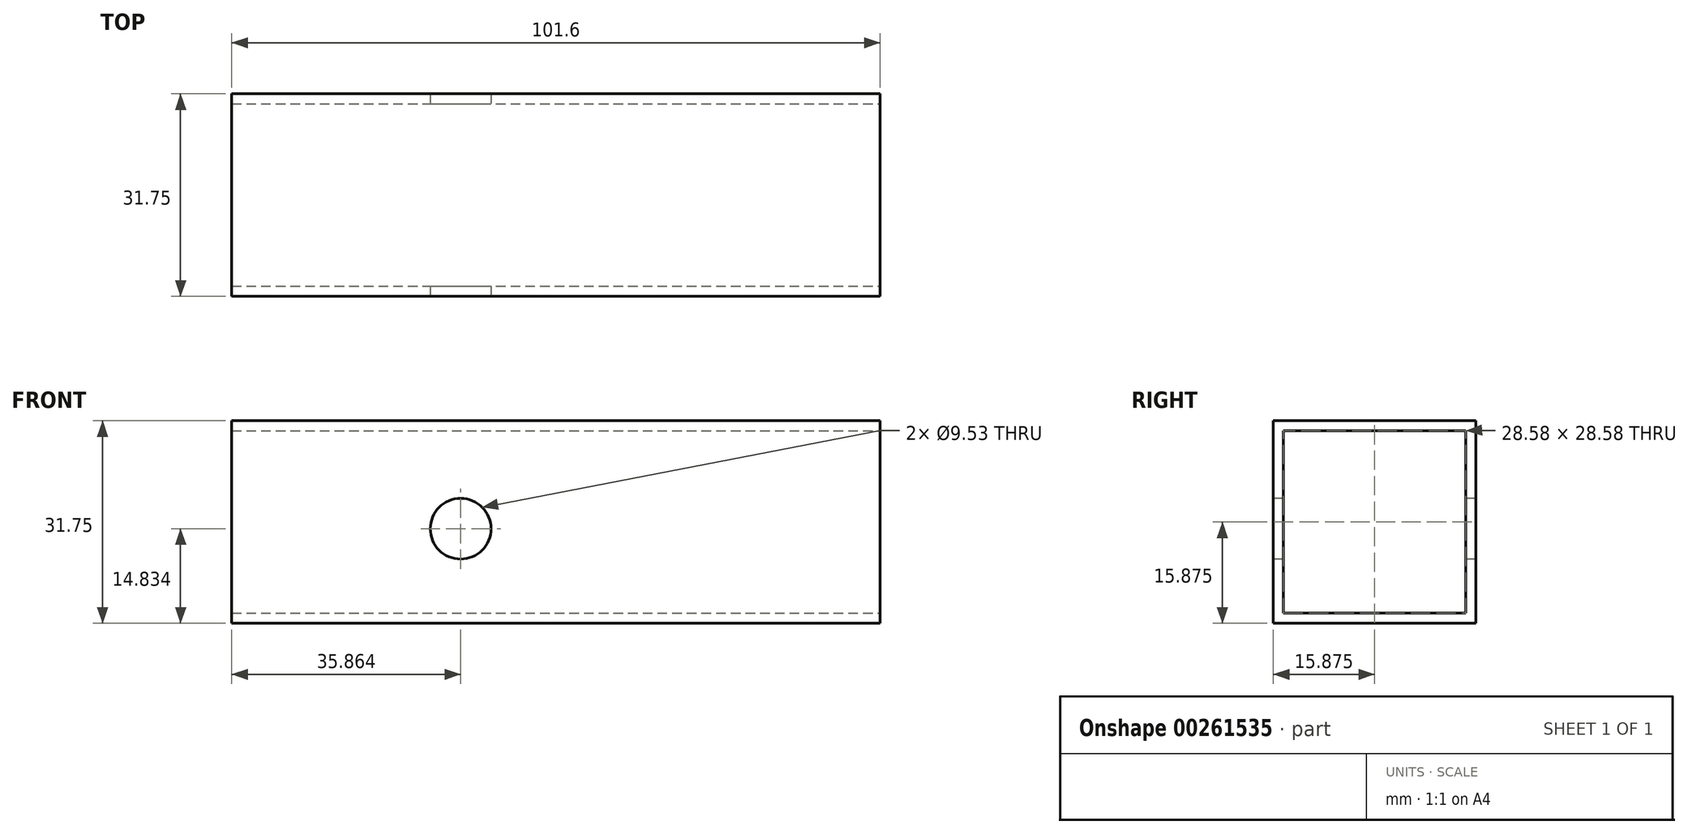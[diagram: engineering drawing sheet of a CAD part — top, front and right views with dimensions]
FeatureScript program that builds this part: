
annotation { "Feature Type Name" : "Feature", "Feature Type Description" : "" }
export const myFeature = defineFeature(function(context is Context, id is Id, definition is map)
    precondition{}
    {
        {
            var Q0;
            Q0=qCreatedBy(makeId("Top.planeOp"),FACE);
            var sketch = newSketch(context, id + "F0", { "sketchPlane" : qUnion([Q0])});
            skLineSegment(sketch, "E0.bottom", {"start": v(0, 0) * mm, "end": v(-101.6, 0) * mm});
            skLineSegment(sketch, "E0.top", {"start": v(0, 31.75) * mm, "end": v(-101.6, 31.75) * mm});
            skLineSegment(sketch, "E0.left", {"start": v(0, 0) * mm, "end": v(0, 31.75) * mm});
            skLineSegment(sketch, "E0.right", {"start": v(-101.6, 0) * mm, "end": v(-101.6, 31.75) * mm});
            skSolve(sketch);
        }
        {
            var Q0;
            Q0=makeQuery(id+"F0.imprint","IMPRINT",FACE,{"disambiguationData":[TD([[makeQuery(id+"F0.imprint","IMPRINT",EDGE,{"derivedFrom":sQuery(id+"F0.wireOp",EDGE,"E0.bottom")}),-1.0]])]});
            extrude(context, id + "F1", {"entities" : qUnion([Q0]), "depth" : 31.75 * mm});
        }
        {
            var Q0;
            Q0=makeQuery(id+"F1.opExtrude","SWEPT_FACE",FACE,{"disambiguationData":[OSD([sQuery(id+"F0.wireOp",EDGE,"E0.right")])]});
            var Q1;
            Q1=makeQuery(id+"F1.opExtrude","SWEPT_FACE",FACE,{"disambiguationData":[OSD([sQuery(id+"F0.wireOp",EDGE,"E0.left")])]});
            shell(context, id + "F2", {"entities" : qUnion([Q0, Q1]), "thickness" : 1.59 * mm});
        }
        {
            var Q0;
            Q0=makeQuery(id+"F1.opExtrude","CAP_FACE",FACE,{"disambiguationData":[OSD([sQuery(id+"F0.wireOp",EDGE,"E0.bottom"),sQuery(id+"F0.wireOp",EDGE,"E0.top"),sQuery(id+"F0.wireOp",EDGE,"E0.left"),sQuery(id+"F0.wireOp",EDGE,"E0.right")])],"isStart":false});
            var sketch = newSketch(context, id + "F3", { "sketchPlane" : qUnion([Q0])});
            skCircle(sketch, "E1", {"center": v(-35.86, 16.92) * mm, "radius": 4.76 * mm});
            skSolve(sketch);
        }
        {
            var Q0;
            Q0=sQuery(id+"F3.wireOp",VERTEX,"E1.center");
            var Q1;
            Q1=makeQuery(id+"F1.opExtrude","SWEPT_BODY",BODY,{"disambiguationData":[OSD([sQuery(id+"F0.wireOp",EDGE,"E0.bottom"),sQuery(id+"F0.wireOp",EDGE,"E0.top"),sQuery(id+"F0.wireOp",EDGE,"E0.left"),sQuery(id+"F0.wireOp",EDGE,"E0.right")])]});
            hole(context, id + "F4", {"style" : HoleStyle.SIMPLE, "endStyle" : HoleEndStyle.THROUGH, "holeDiameter" : 9.52 * mm, "tappedDepth" : 12.7 * mm, "tapClearance" : 3, "locations" : qUnion([Q0]), "scope" : qUnion([Q1])});
        }
        {
            var Q0;
            Q0=makeQuery(id+"F1.opExtrude","SWEPT_BODY",BODY,{"disambiguationData":[OSD([sQuery(id+"F0.wireOp",EDGE,"E0.bottom"),sQuery(id+"F0.wireOp",EDGE,"E0.top"),sQuery(id+"F0.wireOp",EDGE,"E0.left"),sQuery(id+"F0.wireOp",EDGE,"E0.right")])]});
            var Q1;
            Q1=makeQuery(id+"F1.opExtrude","CAP_EDGE",EDGE,{"disambiguationData":[OSD([sQuery(id+"F0.wireOp",EDGE,"E0.top")])],"isStart":false});
            transform(context, id + "F5", {"entities" : qUnion([Q0]), "transformType" : TransformType.ROTATION, "transformAxis" : qUnion([Q1]), "angle" : 90 * degree, "makeCopy" : false});
        }
        {
            var Q0;
            Q0=makeQuery(id+"F1.opExtrude","SWEPT_BODY",BODY,{"disambiguationData":[OSD([sQuery(id+"F0.wireOp",EDGE,"E0.bottom"),sQuery(id+"F0.wireOp",EDGE,"E0.top"),sQuery(id+"F0.wireOp",EDGE,"E0.left"),sQuery(id+"F0.wireOp",EDGE,"E0.right")])]});
            var Q1;
            Q1=makeQuery(id+"F1.opExtrude","CAP_EDGE",EDGE,{"disambiguationData":[OSD([sQuery(id+"F0.wireOp",EDGE,"E0.right")])],"isStart":true});
            transform(context, id + "F6", {"entities" : qUnion([Q0]), "transformType" : TransformType.ROTATION, "transformAxis" : qUnion([Q1]), "angle" : 180 * degree, "makeCopy" : false});
        }
    });
